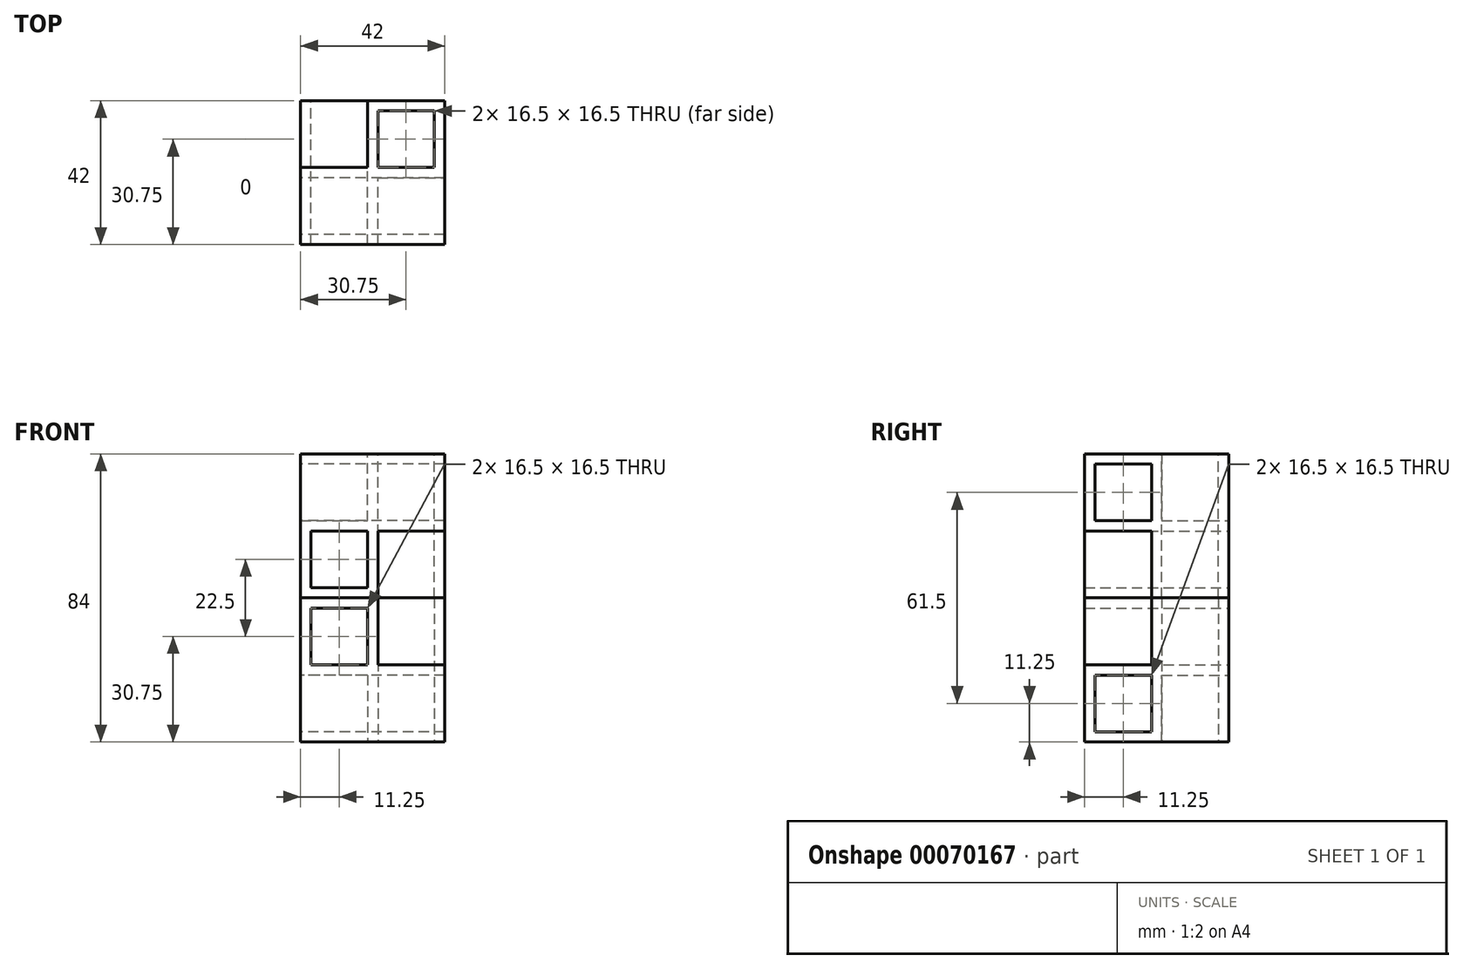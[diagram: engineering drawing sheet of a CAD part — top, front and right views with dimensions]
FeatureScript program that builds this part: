
annotation { "Feature Type Name" : "Feature", "Feature Type Description" : "" }
export const myFeature = defineFeature(function(context is Context, id is Id, definition is map)
    precondition{}
    {
        {
            var Q0;
            Q0=qCreatedBy(makeId("Front.planeOp"),FACE);
            var sketch = newSketch(context, id + "F0", { "sketchPlane" : qUnion([Q0])});
            skLineSegment(sketch, "E0.bottom", {"start": v(-19.5, 19.5) * mm, "end": v(-3, 19.5) * mm});
            skLineSegment(sketch, "E0.top", {"start": v(-19.5, 3) * mm, "end": v(-3, 3) * mm});
            skLineSegment(sketch, "E0.left", {"start": v(-19.5, 19.5) * mm, "end": v(-19.5, 3) * mm});
            skLineSegment(sketch, "E0.right", {"start": v(-3, 19.5) * mm, "end": v(-3, 3) * mm});
            skLineSegment(sketch, "E1.0", {"start": v(-22.5, 0) * mm, "end": v(0, 0) * mm});
            skLineSegment(sketch, "E1.1", {"start": v(-22.5, 22.5) * mm, "end": v(-22.5, 0) * mm});
            skLineSegment(sketch, "E1.2", {"start": v(-22.5, 22.5) * mm, "end": v(0, 22.5) * mm});
            skLineSegment(sketch, "E1.3", {"start": v(0, 22.5) * mm, "end": v(0, 0) * mm});
            skSolve(sketch);
        }
        {
            var Q0;
            Q0 = qSketchRegion(id + "F0", true);
            extrude(context, id + "F1", {"entities" : qUnion([Q0]), "depth" : 42 * mm});
        }
        {
            var Q0;
            Q0=makeQuery(id+"F1.opExtrude","SWEPT_FACE",FACE,{"disambiguationData":[OSD([sQuery(id+"F0.wireOp",EDGE,"E1.1")])]});
            var sketch = newSketch(context, id + "F2", { "sketchPlane" : qUnion([Q0])});
            skLineSegment(sketch, "E2.bottom", {"start": v(22.5, 39) * mm, "end": v(39, 39) * mm});
            skLineSegment(sketch, "E2.top", {"start": v(22.5, 22.5) * mm, "end": v(39, 22.5) * mm});
            skLineSegment(sketch, "E2.left", {"start": v(22.5, 39) * mm, "end": v(22.5, 22.5) * mm});
            skLineSegment(sketch, "E2.right", {"start": v(39, 39) * mm, "end": v(39, 22.5) * mm});
            skLineSegment(sketch, "E3.0", {"start": v(19.5, 42) * mm, "end": v(19.5, 19.5) * mm});
            skLineSegment(sketch, "E3.1", {"start": v(19.5, 42) * mm, "end": v(42, 42) * mm});
            skLineSegment(sketch, "E3.2", {"start": v(42, 42) * mm, "end": v(42, 19.5) * mm});
            skLineSegment(sketch, "E3.3", {"start": v(19.5, 19.5) * mm, "end": v(42, 19.5) * mm});
            skSolve(sketch);
        }
        {
            var Q0;
            Q0 = qSketchRegion(id + "F2", true);
            extrude(context, id + "F3", {"entities" : qUnion([Q0]), "operationType" : NewBodyOperationType.ADD, "oppositeDirection" : true, "depth" : 42 * mm});
        }
        {
            var Q0;
            Q0=makeQuery(id+"F3.opExtrude","SWEPT_FACE",FACE,{"disambiguationData":[OSD([sQuery(id+"F2.wireOp",EDGE,"E3.1")])]});
            var sketch = newSketch(context, id + "F4", { "sketchPlane" : qUnion([Q0])});
            skLineSegment(sketch, "E4.bottom", {"start": v(16.5, -3) * mm, "end": v(0, -3) * mm});
            skLineSegment(sketch, "E4.top", {"start": v(16.5, -19.5) * mm, "end": v(0, -19.5) * mm});
            skLineSegment(sketch, "E4.left", {"start": v(16.5, -3) * mm, "end": v(16.5, -19.5) * mm});
            skLineSegment(sketch, "E4.right", {"start": v(0, -3) * mm, "end": v(0, -19.5) * mm});
            skLineSegment(sketch, "E5.0", {"start": v(-3, 0) * mm, "end": v(-3, -22.5) * mm});
            skLineSegment(sketch, "E5.1", {"start": v(19.5, 0) * mm, "end": v(-3, 0) * mm});
            skLineSegment(sketch, "E5.2", {"start": v(19.5, 0) * mm, "end": v(19.5, -22.5) * mm});
            skLineSegment(sketch, "E5.3", {"start": v(19.5, -22.5) * mm, "end": v(-3, -22.5) * mm});
            skSolve(sketch);
        }
        {
            var Q0;
            Q0 = qSketchRegion(id + "F4", true);
            extrude(context, id + "F5", {"entities" : qUnion([Q0]), "operationType" : NewBodyOperationType.ADD, "oppositeDirection" : true, "depth" : 42 * mm});
        }
        {
            var Q0;
            Q0=makeQuery(id+"F1.opExtrude","SWEPT_BODY",BODY,{"disambiguationData":[OSD([sQuery(id+"F0.wireOp",EDGE,"E0.bottom"),sQuery(id+"F0.wireOp",EDGE,"E0.top"),sQuery(id+"F0.wireOp",EDGE,"E0.left"),sQuery(id+"F0.wireOp",EDGE,"E0.right"),sQuery(id+"F0.wireOp",EDGE,"E1.0"),sQuery(id+"F0.wireOp",EDGE,"E1.1"),sQuery(id+"F0.wireOp",EDGE,"E1.2"),sQuery(id+"F0.wireOp",EDGE,"E1.3")])]});
            var Q1;
            Q1=qCreatedBy(makeId("Top.planeOp"),FACE);
            mirror(context, id + "F6", {"entities" : qUnion([Q0]), "mirrorPlane" : qUnion([Q1])});
        }
    });
